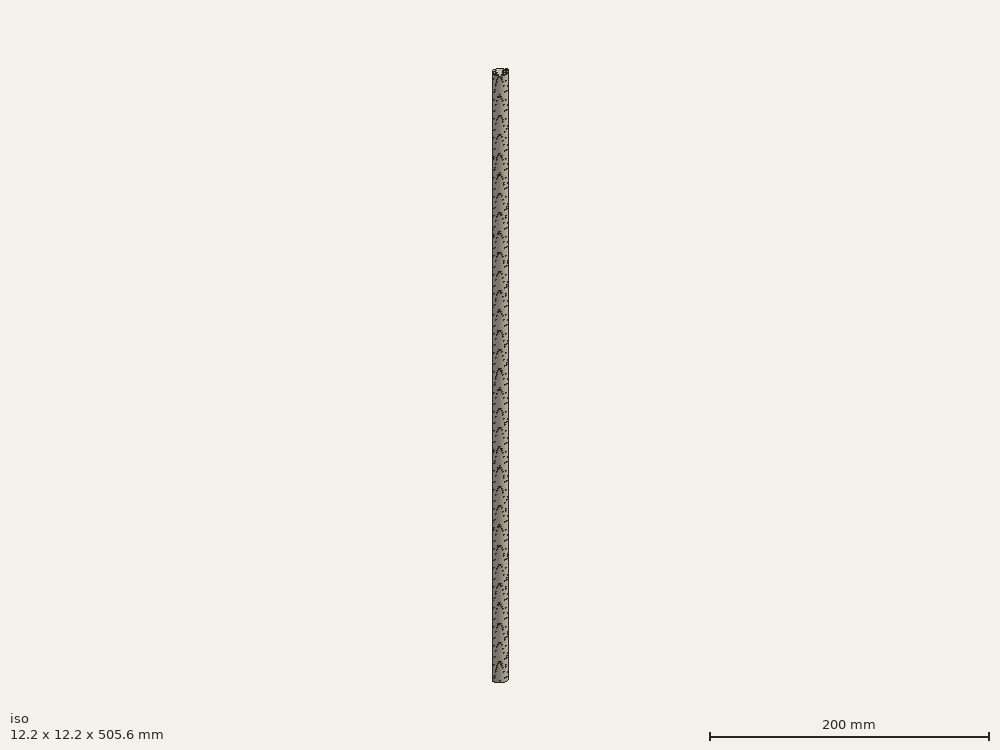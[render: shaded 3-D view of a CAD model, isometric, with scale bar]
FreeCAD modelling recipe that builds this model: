
FCSTD DOCUMENT  (FreeCAD 0.16R6386 (Git))
Label: SinFin
License: All rights reserved
LicenseURL: http://es.wikipedia.org/wiki/Todos_los_derechos_reservados
objects: Part::Feature×3, Sketcher::SketchObject×2, PartDesign::Chamfer×2, PartDesign::Pad×1, Part::Sweep×1
note: 10 computed .brp shape members not serialized (recipe doc carries the construction recipe); baked Part::Feature solids carry a one-line shape summary decoded from their .brp

FEATURE [Sketcher::SketchObject] Sketch
  sketch-geometry (1):
    g0: Circle CenterX=0 CenterY=0 CenterZ=0 NormalX=0 NormalY=0 NormalZ=1 Radius=6
  constraints (2):
    c: Coincident(g0,g-1)
    c: Radius(g0) = 6
FEATURE [PartDesign::Pad] Pad
  Length = 485
  Length2 = 100
  Sketch = -> Sketch
  Type = 0
FEATURE [PartDesign::Chamfer] Chamfer
  Base = -> Pad [Edge2]
  Size = 1.75
FEATURE [PartDesign::Chamfer] Chamfer001
  Base = -> Chamfer [Edge3]
  Size = 1.75
FEATURE [Part::Feature] Shape
  shape: bbox 12 x 12 x 504 mm, 0 faces, 0 solids (baked)
FEATURE [Sketcher::SketchObject] Sketch001
  Placement = pos=(0,0,0) rot=(-1,0,0;4.71239rad)
  sketch-geometry (4):
    g0: LineSegment StartX=5.053 StartY=0.21875 StartZ=0 EndX=5.053 EndY=-0.21875 EndZ=0
    g1: LineSegment StartX=5.053 StartY=-0.21875 StartZ=0 EndX=6.1 EndY=-0.823236 EndZ=0
    g2: LineSegment StartX=6.1 StartY=-0.823236 StartZ=0 EndX=6.1 EndY=0.823236 EndZ=0
    g3: LineSegment StartX=6.1 StartY=0.823236 StartZ=0 EndX=5.053 EndY=0.21875 EndZ=0
  constraints (12):
    c: Vertical(g0)
    c: Coincident(g0,g1)
    c: Coincident(g1,g2)
    c: Vertical(g2)
    c: Coincident(g2,g3)
    c: Coincident(g3,g0)
    c: Symmetric(g0,g0,g-1)
    c: Symmetric(g2,g1,g-1)
    c: Angle(g1,g3) = 1.0472
    c: DistanceY(g0,g0) = -0.4375
    c: DistanceX(g-1,g0) = 5.053
    c: DistanceX(g-1,g1) = 6.1
FEATURE [Part::Sweep] Sweep
  Frenet = true
  Sections = -> [Sketch001]
  Solid = true
  Spine = -> Shape [Edge1]
  Transition = 1
FEATURE [Part::Feature] Chamfer001001  label="Chamfer002"
  shape: bbox 12 x 12 x 485 mm, 5 faces (baked)
FEATURE [Part::Feature] Sweep001
  shape: bbox 14.35 x 14.35 x 505.6 mm, 6 faces (baked)
